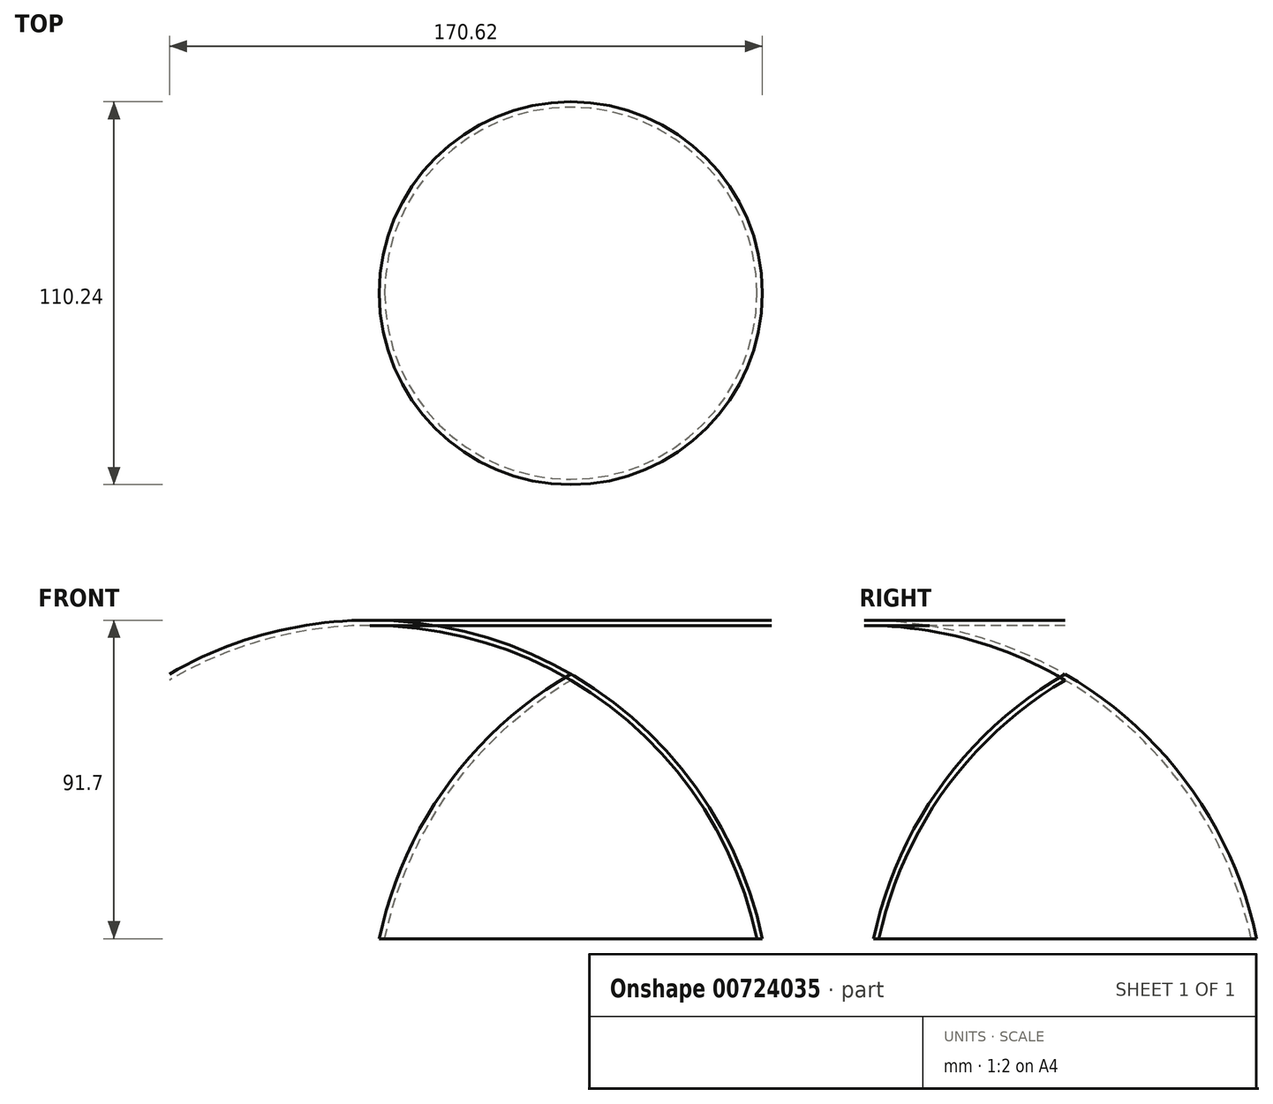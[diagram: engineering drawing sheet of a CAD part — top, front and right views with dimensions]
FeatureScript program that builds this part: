
annotation { "Feature Type Name" : "Feature", "Feature Type Description" : "" }
export const myFeature = defineFeature(function(context is Context, id is Id, definition is map)
    precondition{}
    {
        {
            var Q0;
            Q0=qCreatedBy(makeId("Front.planeOp"),FACE);
            var sketch = newSketch(context, id + "F0", { "sketchPlane" : qUnion([Q0])});
            skLineSegment(sketch, "E0", {"start": v(0, 0) * mm, "end": v(0, 76.2) * mm});
            skLineSegment(sketch, "E1", {"start": v(0, 0) * mm, "end": v(55.12, 0) * mm});
            skArc(sketch, "E2", {"start": v(55.12, 0) * mm, "mid": v(35.68, 43.97) * mm, "end": v(0, 76.2) * mm});
            skSolve(sketch);
        }
        {
            var Q0;
            Q0 = qSketchRegion(id + "F0", true);
            var Q1;
            Q1=sQuery(id+"F0.wireOp",EDGE,"E0");
            revolve(context, id + "F1", {"surfaceOperationType" : NewSurfaceOperationType.NEW, "entities" : qUnion([Q0]), "axis" : qUnion([Q1]), "revolveType" : RevolveType.FULL});
        }
        {
            var Q0;
            Q0=makeQuery(id+"F1.opRevolve","SWEPT_FACE",FACE,{"disambiguationData":[OSD([sQuery(id+"F0.wireOp",EDGE,"E1")])]});
            shell(context, id + "F2", {"entities" : qUnion([Q0]), "thickness" : 1.52 * mm});
        }
    });
